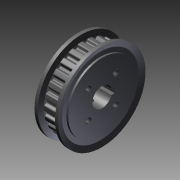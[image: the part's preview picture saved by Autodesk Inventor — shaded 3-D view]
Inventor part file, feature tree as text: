
AUTODESK INVENTOR PART (.ipt)
format: ipt  version: 2011 SP1 (Build 150282100, 282)  size: 556,544 bytes
history: native  units: mm
features: other x14, revolve x4, hole x2, extrude x2, thread x2, sketch x2, pattern_linear x1
ambient origin geometry x8: Origin, YZ Plane, XZ Plane, XY Plane, X Axis, Y Axis, Z Axis, Center Point
bodies: Solid1 (feature_tree)
feature tree (27):
  revolve  "Revolution1"  [1 undecoded]
  hole  "Hole1"  [1 undecoded]
  extrude  "Extrusion1"  TaperAngle=360.0deg  [1 undecoded]
  extrude  "Extrusion2"  TaperAngle=360.0deg  [1 undecoded]
  revolve  "Revolution2"  [1 undecoded]
  revolve  "Revolution3"  Angle=360.0deg
  thread  "Thread1"  [1 undecoded]
  revolve  "Revolution4"  [1 undecoded]
  thread  "Thread2"  [1 undecoded]
  hole  "Hole2"  [1 undecoded]
  pattern_linear  "Rectangular Pattern1"  [2 undecoded]
  other  "to_screw1_XY"
  other  "to_screw1_YZ"
  other  "to_screw1_ZX"
  other  "to_screw1_X"
  other  "to_screw1_Y"
  other  "to_screw1_Z"
  other  "to_screw1_Center"
  other  "to_screw2_XY"
  other  "to_screw2_YZ"
  other  "to_screw2_ZX"
  other  "to_screw2_X"
  other  "to_screw2_Y"
  other  "to_screw2_Z"
  other  "to_screw2_Center"
  sketch  "Sketch2"  dims[d0=360.0deg]
  sketch  "Sketch8"  dims[d1=10.0mm d2=6.0mm d3=4.0mm d4=2.0mm d5=90.0deg d6=12.5mm d7=0.0mm d8=7.5mm d9=0.0mm d10=12.5mm d11=0.0mm d12=360.0deg d13=360.0deg d14=13.56mm d15=0.0mm d16=360.0deg d17=14.96mm d18=0.0mm d19=2.459mm d20=6.2705mm d21=3.0mm d22=2.0mm d23=90.0deg d24=8.790148mm d25=120.0deg d26=20.0mm d28=14.142136mm d29=20.0mm d31=14.142136mm d32=0.0mm]
note: 11 required parameter values undecoded (feature->parameter linkage not recoverable at this tier; creation-order binding heuristic only, values carry confidence <= 0.55)